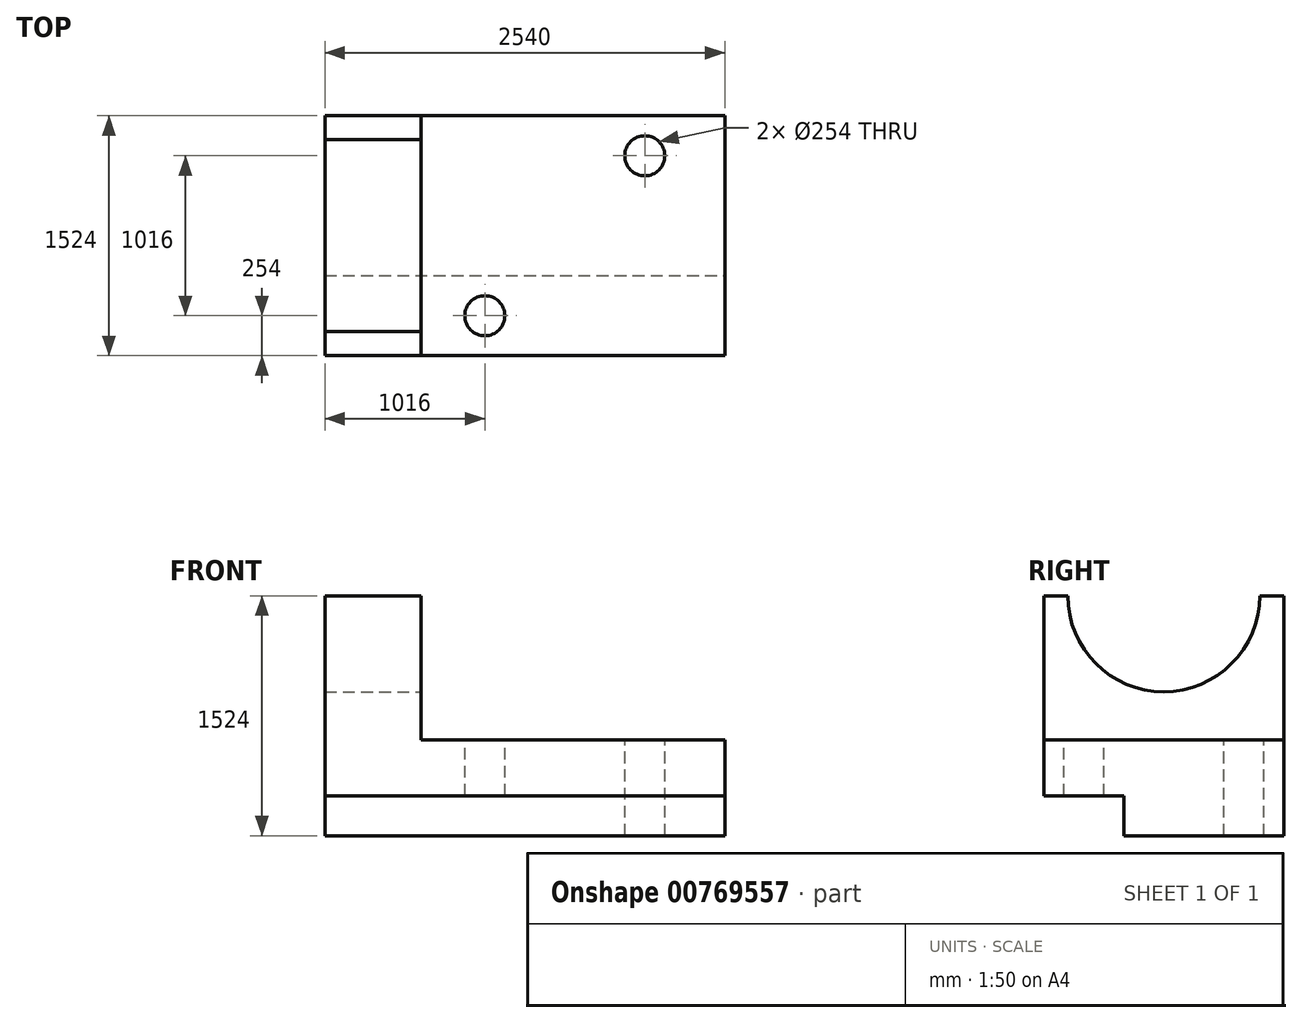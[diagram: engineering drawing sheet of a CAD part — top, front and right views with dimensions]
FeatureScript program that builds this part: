
annotation { "Feature Type Name" : "Feature", "Feature Type Description" : "" }
export const myFeature = defineFeature(function(context is Context, id is Id, definition is map)
    precondition{}
    {
        {
            var Q0;
            Q0=qCreatedBy(makeId("Front.planeOp"),FACE);
            var sketch = newSketch(context, id + "F0", { "sketchPlane" : qUnion([Q0])});
            skLineSegment(sketch, "E0.bottom", {"start": v(0, 0) * mm, "end": v(2540, 0) * mm});
            skLineSegment(sketch, "E0.top", {"start": v(0, 1524) * mm, "end": v(2540, 1524) * mm});
            skLineSegment(sketch, "E0.left", {"start": v(0, 0) * mm, "end": v(0, 1524) * mm});
            skLineSegment(sketch, "E0.right", {"start": v(2540, 0) * mm, "end": v(2540, 1524) * mm});
            skSolve(sketch);
        }
        {
            var Q0;
            Q0=makeQuery(id+"F0.imprint","IMPRINT",FACE,{"disambiguationData":[TD([[makeQuery(id+"F0.imprint","IMPRINT",EDGE,{"derivedFrom":sQuery(id+"F0.wireOp",EDGE,"E0.bottom")}),1.0]])]});
            extrude(context, id + "F1", {"entities" : qUnion([Q0]), "depth" : 1524 * mm, "offsetDistance" : 25.4 * mm});
        }
        {
            var Q0;
            Q0=makeQuery(id+"F1.opExtrude","CAP_FACE",FACE,{"disambiguationData":[OSD([sQuery(id+"F0.wireOp",EDGE,"E0.bottom"),sQuery(id+"F0.wireOp",EDGE,"E0.top"),sQuery(id+"F0.wireOp",EDGE,"E0.left"),sQuery(id+"F0.wireOp",EDGE,"E0.right")])],"isStart":false});
            var sketch = newSketch(context, id + "F2", { "sketchPlane" : qUnion([Q0])});
            skLineSegment(sketch, "E1", {"start": v(2540, 609.6) * mm, "end": v(609.6, 609.6) * mm});
            skLineSegment(sketch, "E2", {"start": v(609.6, 609.6) * mm, "end": v(609.6, 1524) * mm});
            skLineSegment(sketch, "E3", {"start": v(2540, 609.6) * mm, "end": v(2540, 0) * mm});
            skSolve(sketch);
        }
        {
            var Q0;
            {var subQ0=sQuery(id+"F2.wireOp",EDGE,"E1");Q0=makeQuery(id+"F2.imprint","IMPRINT",FACE,{"disambiguationData":[TD([[makeQuery(id+"F2.imprint","IMPRINT",EDGE,{"derivedFrom":subQ0}),-1.0]])]});}
            extrude(context, id + "F3", {"entities" : qUnion([Q0]), "operationType" : NewBodyOperationType.REMOVE, "oppositeDirection" : true, "depth" : 1524 * mm, "offsetDistance" : 25.4 * mm});
        }
        {
            var Q0;
            Q0=makeQuery(id+"F1.opExtrude","SWEPT_FACE",FACE,{"disambiguationData":[OSD([sQuery(id+"F0.wireOp",EDGE,"E0.right")])]});
            var sketch = newSketch(context, id + "F4", { "sketchPlane" : qUnion([Q0])});
            skLineSegment(sketch, "E4", {"start": v(-1524, 254) * mm, "end": v(-1016, 254) * mm});
            skLineSegment(sketch, "E5", {"start": v(-1016, 254) * mm, "end": v(-1016, 0) * mm});
            skSolve(sketch);
        }
        {
            var Q0;
            {var subQ0=sQuery(id+"F4.wireOp",EDGE,"E4");Q0=makeQuery(id+"F4.imprint","IMPRINT",FACE,{"disambiguationData":[TD([[makeQuery(id+"F4.imprint","IMPRINT",EDGE,{"derivedFrom":subQ0}),-1.0]])]});}
            extrude(context, id + "F5", {"entities" : qUnion([Q0]), "operationType" : NewBodyOperationType.REMOVE, "oppositeDirection" : true, "depth" : 2540 * mm, "offsetDistance" : 25.4 * mm});
        }
        {
            var Q0;
            Q0=makeQuery(id+"F3.boolean.opBoolean","COPY",FACE,{"derivedFrom":makeQuery(id+"F3.opExtrude","SWEPT_FACE",FACE,{"disambiguationData":[OSD([sQuery(id+"F2.wireOp",EDGE,"E2")])]})});
            var sketch = newSketch(context, id + "F6", { "sketchPlane" : qUnion([Q0])});
            skLineSegment(sketch, "E6", {"start": v(-1524, 1524) * mm, "end": v(-762, 1524) * mm});
            skCircle(sketch, "E7", {"center": v(-762, 1524) * mm, "radius": 609.6 * mm});
            skSolve(sketch);
        }
        {
            var Q0;
            {var subQ0=sQuery(id+"F6.wireOp",EDGE,"E6");var subQ3=sQuery(id+"F6.wireOp",EDGE,"E7");var subQ4=makeQuery(id+"F6.imprint","INTERSECT",VERTEX,{"derivedFrom":[subQ0,subQ3]});Q0=makeQuery(id+"F6.imprint","IMPRINT",FACE,{"disambiguationData":[TD([[makeQuery(id+"F6.imprint","IMPRINT",EDGE,{"disambiguationData":[TD([[subQ4,1.0]])],"derivedFrom":subQ0}),1.0]])]});}
            extrude(context, id + "F7", {"entities" : qUnion([Q0]), "operationType" : NewBodyOperationType.REMOVE, "oppositeDirection" : true, "depth" : 609.6 * mm, "offsetDistance" : 25.4 * mm});
        }
        {
            var Q0;
            Q0=makeQuery(id+"F3.boolean.opBoolean","COPY",FACE,{"derivedFrom":makeQuery(id+"F3.opExtrude","SWEPT_FACE",FACE,{"disambiguationData":[OSD([sQuery(id+"F2.wireOp",EDGE,"E1")])]})});
            var sketch = newSketch(context, id + "F8", { "sketchPlane" : qUnion([Q0])});
            skLineSegment(sketch, "E8", {"start": v(609.6, -1270) * mm, "end": v(1016, -1270) * mm});
            skLineSegment(sketch, "E9", {"start": v(1016, -1270) * mm, "end": v(1016, -1524) * mm});
            skLineSegment(sketch, "E10", {"start": v(2032, 0) * mm, "end": v(2032, -254) * mm});
            skLineSegment(sketch, "E11", {"start": v(2032, -254) * mm, "end": v(2540, -254) * mm});
            skCircle(sketch, "E12", {"center": v(1016, -1270) * mm, "radius": 127 * mm});
            skCircle(sketch, "E13", {"center": v(2032, -254) * mm, "radius": 127 * mm});
            skSolve(sketch);
        }
        {
            var Q0;
            {var subQ0=sQuery(id+"F8.wireOp",EDGE,"E9");var subQ1=sQuery(id+"F8.wireOp",EDGE,"E8");var subQ2=makeQuery(id+"F8.imprint","INTERSECT",VERTEX,{"derivedFrom":[subQ1,subQ0]});Q0=makeQuery(id+"F8.imprint","IMPRINT",FACE,{"disambiguationData":[TD([[makeQuery(id+"F8.imprint","IMPRINT",EDGE,{"disambiguationData":[TD([[subQ2,1.0]])],"derivedFrom":subQ1}),-1.0]])]});}
            var Q1;
            {var subQ0=sQuery(id+"F8.wireOp",EDGE,"E9");var subQ1=sQuery(id+"F8.wireOp",EDGE,"E8");var subQ2=makeQuery(id+"F8.imprint","INTERSECT",VERTEX,{"derivedFrom":[subQ1,subQ0]});Q1=makeQuery(id+"F8.imprint","IMPRINT",FACE,{"disambiguationData":[TD([[makeQuery(id+"F8.imprint","IMPRINT",EDGE,{"disambiguationData":[TD([[subQ2,1.0]])],"derivedFrom":subQ1}),1.0]])]});}
            var Q2;
            {var subQ0=sQuery(id+"F8.wireOp",EDGE,"E11");var subQ1=sQuery(id+"F8.wireOp",EDGE,"E10");var subQ2=makeQuery(id+"F8.imprint","INTERSECT",VERTEX,{"derivedFrom":[subQ1,subQ0]});Q2=makeQuery(id+"F8.imprint","IMPRINT",FACE,{"disambiguationData":[TD([[makeQuery(id+"F8.imprint","IMPRINT",EDGE,{"disambiguationData":[TD([[subQ2,1.0]])],"derivedFrom":subQ1}),-1.0]])]});}
            var Q3;
            {var subQ0=sQuery(id+"F8.wireOp",EDGE,"E11");var subQ1=sQuery(id+"F8.wireOp",EDGE,"E10");var subQ2=makeQuery(id+"F8.imprint","INTERSECT",VERTEX,{"derivedFrom":[subQ1,subQ0]});Q3=makeQuery(id+"F8.imprint","IMPRINT",FACE,{"disambiguationData":[TD([[makeQuery(id+"F8.imprint","IMPRINT",EDGE,{"disambiguationData":[TD([[subQ2,1.0]])],"derivedFrom":subQ1}),1.0]])]});}
            extrude(context, id + "F9", {"entities" : qUnion([Q0, Q1, Q2, Q3]), "operationType" : NewBodyOperationType.REMOVE, "oppositeDirection" : true, "depth" : 609.6 * mm, "offsetDistance" : 25.4 * mm});
        }
    });
